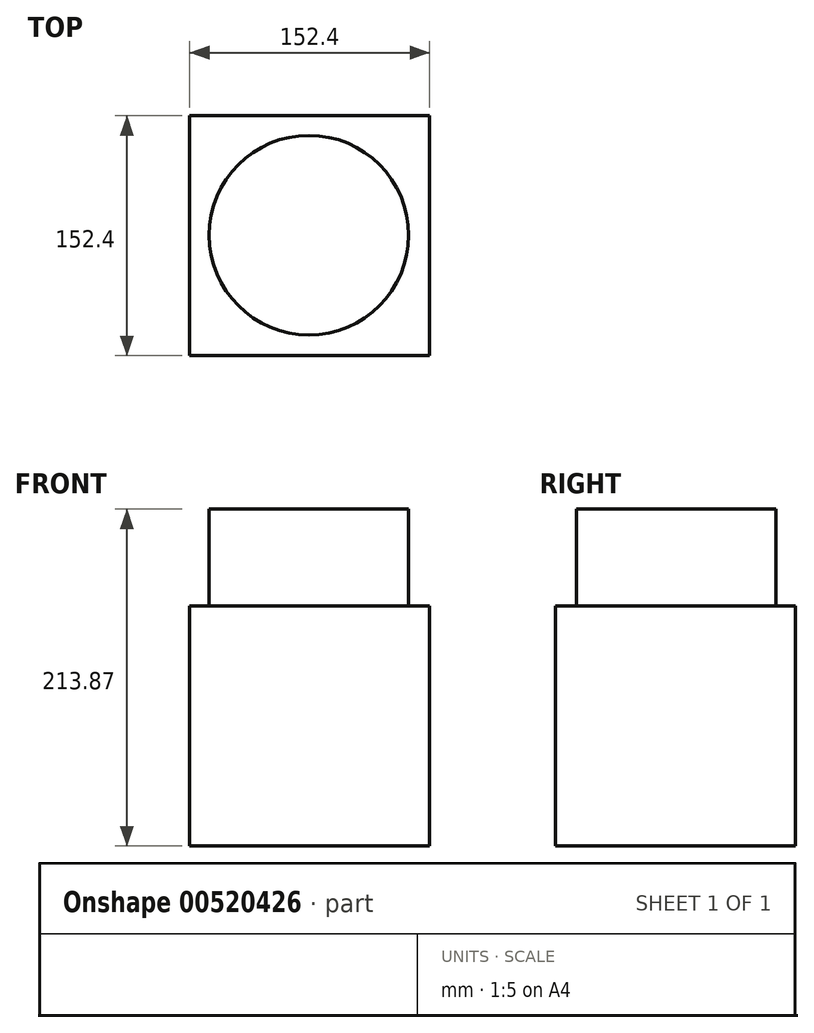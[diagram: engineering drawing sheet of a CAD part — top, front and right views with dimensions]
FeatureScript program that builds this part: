
annotation { "Feature Type Name" : "Feature", "Feature Type Description" : "" }
export const myFeature = defineFeature(function(context is Context, id is Id, definition is map)
    precondition{}
    {
        {
            var Q0;
            Q0=qCreatedBy(makeId("Top.planeOp"),FACE);
            var sketch = newSketch(context, id + "F0", { "sketchPlane" : qUnion([Q0])});
            skLineSegment(sketch, "E0.bottom", {"start": v(76.7, -55.26) * mm, "end": v(-75.7, -55.26) * mm});
            skLineSegment(sketch, "E0.top", {"start": v(76.7, 97.14) * mm, "end": v(-75.7, 97.14) * mm});
            skLineSegment(sketch, "E0.left", {"start": v(76.7, -55.26) * mm, "end": v(76.7, 97.14) * mm});
            skLineSegment(sketch, "E0.right", {"start": v(-75.7, -55.26) * mm, "end": v(-75.7, 97.14) * mm});
            skPoint(sketch, "E1.center.orphan", {"position": v(0, 13.74) * mm});
            skSolve(sketch);
        }
        {
            var Q0;
            Q0 = qSketchRegion(id + "F0", true);
            extrude(context, id + "F1", {"entities" : qUnion([Q0]), "depth" : 152.4 * mm, "offsetDistance" : 25.4 * mm});
        }
        {
            var Q0;
            Q0=makeQuery(id+"F1.opExtrude","CAP_FACE",FACE,{"disambiguationData":[OSD([sQuery(id+"F0.wireOp",EDGE,"E0.bottom"),sQuery(id+"F0.wireOp",EDGE,"E0.top"),sQuery(id+"F0.wireOp",EDGE,"E0.left"),sQuery(id+"F0.wireOp",EDGE,"E0.right"),sQuery(id+"F0.wireOp",EDGE,"E1")])],"isStart":false});
            var sketch = newSketch(context, id + "F2", { "sketchPlane" : qUnion([Q0])});
            skCircle(sketch, "E2", {"center": v(0, 21.27) * mm, "radius": 63.37 * mm});
            skSolve(sketch);
        }
        {
            var Q0;
            Q0=makeQuery(id+"F2.imprint","IMPRINT",FACE,{"disambiguationData":[TD([[makeQuery(id+"F2.imprint","IMPRINT",EDGE,{"derivedFrom":sQuery(id+"F2.wireOp",EDGE,"E2")}),1.0]])]});
            extrude(context, id + "F3", {"entities" : qUnion([Q0]), "operationType" : NewBodyOperationType.ADD, "depth" : 61.47 * mm, "offsetDistance" : 25.4 * mm});
        }
    });
